# Revit family: Lighting-StreetLighting-GEWISS-STREET[O3]-SINGLE_HEAD_BRACKET
name_source: partatom
category: Apparecchi per illuminazione
units: mm (PartAtom-declared; Revit-internal decimal feet)

## family parameters
Basato su piano di lavoro = Sì
Condiviso = No
Numero OmniClass = 23.80.00.00
Punto di calcolo locali = No
Quota connettore circolare = Usa diametro
Sempre verticale = No
Sorgente d'illuminazione = No
Taglio con vuoti quando caricato = No
Tipo di parte = Normale
Titolo OmniClass = Electric Power and Lighting

## types (1)
- GW87581 - Galvanised steel - Grey - Single
    Altezza da terra testa staffa = 822 mm
    Catalogue = LIGHTING
    Catalogue Range = STREET [O3]
    Colour = Graphite grey
    Description: = Single pole head bracket
    Descrizione = STREET SINGLE POLE HEAD BRACKET GR. GREY
    Dimension = Ã˜ 60mm
    Dimensions (mm) = Ã˜ 60mm
    EAN code = 8011564783034
    Electrocod = 240
    IDF = 2fe635a5-cec3-4f8c-9283-e615bd95f4cd
    IDT = 92612c42-9c0e-491e-a234-09077f2a4f14
    Immagine tipo = GW87581.jpg
    L_staffa = 120 mm  [stored 0.393701 ft]
    Length = 1 m
    Material = Galvanised steel
    Modello = GW87581
    Produttore = GEWISS S.p.A.
    Prospetto di default = 1219 mm
    SEO = Bracket
    Supporti = <Per categoria>
    Technical sheet = https://www.gewiss.com
    Tubolare = <Per categoria>
    URL = https://www.gewiss.com
    Version file RFA = 20.11
    Weight (kg) = 8
    Weight (kg): = 8

note: [stored X ft] marks values corroborated as IEEE doubles in the binary element streams (Revit-internal decimal feet)

## geometry (parser evidence)
native form markers: Blend x4
no freeform markers — native parametric forms only
